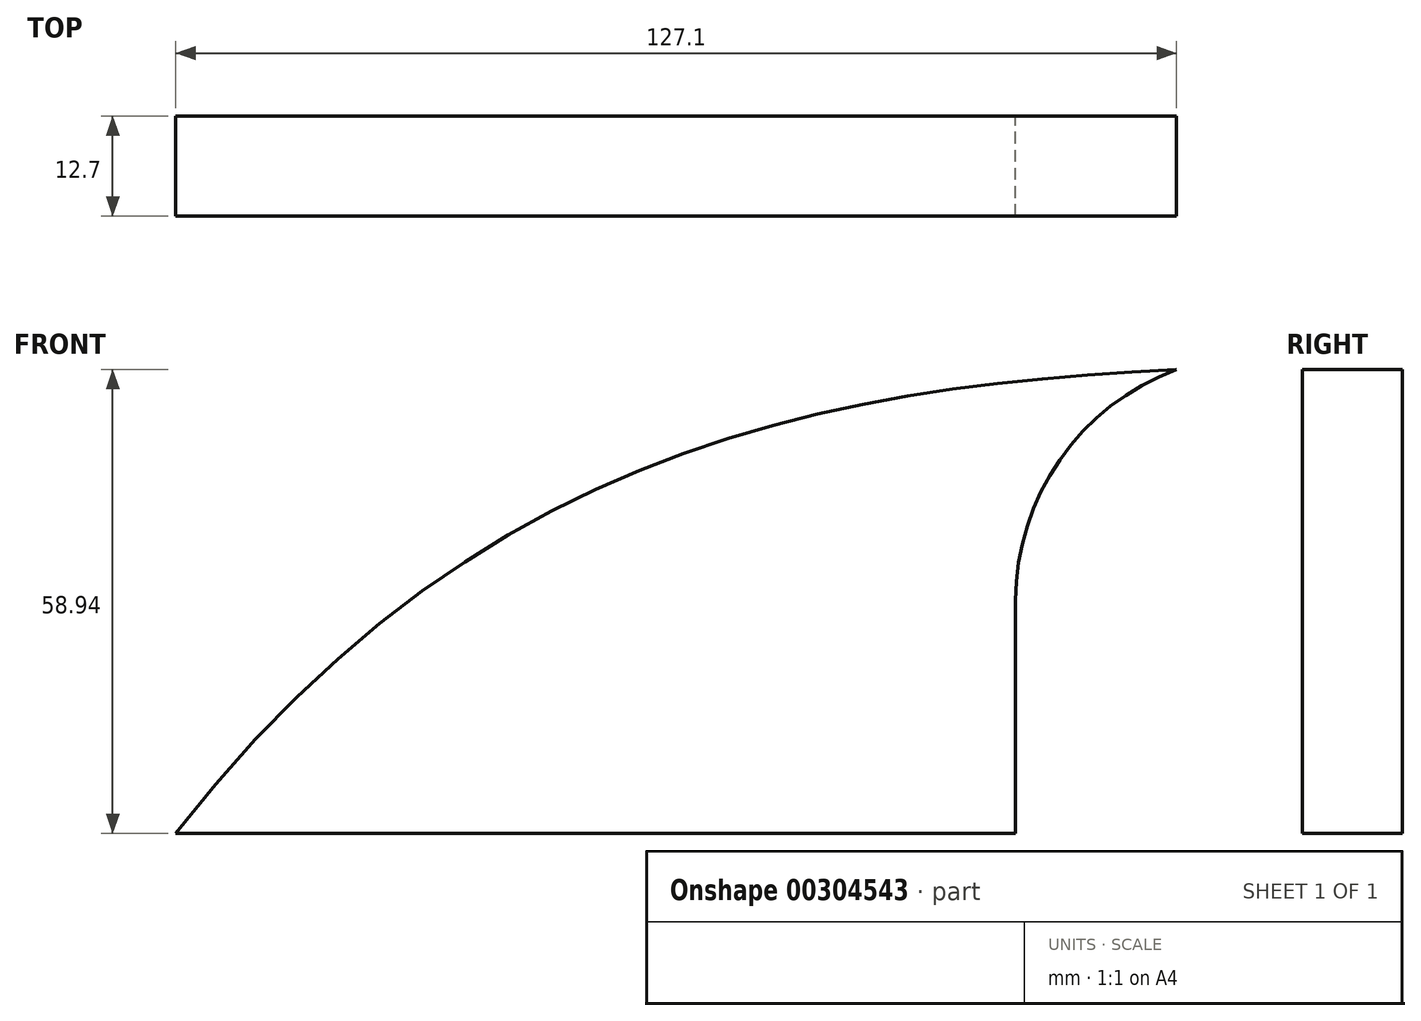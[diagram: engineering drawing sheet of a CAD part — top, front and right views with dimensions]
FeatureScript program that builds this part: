
annotation { "Feature Type Name" : "Feature", "Feature Type Description" : "" }
export const myFeature = defineFeature(function(context is Context, id is Id, definition is map)
    precondition{}
    {
        {
            var Q0;
            Q0=qCreatedBy(makeId("Front.planeOp"),FACE);
            var sketch = newSketch(context, id + "F0", { "sketchPlane" : qUnion([Q0])});
            skLineSegment(sketch, "E0.bottom", {"start": v(63.5, 25.4) * mm, "end": v(-63.5, 25.4) * mm});
            skLineSegment(sketch, "E0.top", {"start": v(63.5, -25.4) * mm, "end": v(-63.5, -25.4) * mm});
            skLineSegment(sketch, "E0.left", {"start": v(63.5, 25.4) * mm, "end": v(63.5, -25.4) * mm});
            skLineSegment(sketch, "E0.right", {"start": v(-63.5, 25.4) * mm, "end": v(-63.5, -25.4) * mm});
            skPoint(sketch, "E0.middle", {"position": v(0, 0) * mm});
            skLineSegment(sketch, "E1.bottom", {"start": v(201.55, 89.46) * mm, "end": v(131.27, 89.46) * mm});
            skLineSegment(sketch, "E1.top", {"start": v(201.55, 51.36) * mm, "end": v(131.27, 51.36) * mm});
            skLineSegment(sketch, "E1.left", {"start": v(201.55, 89.46) * mm, "end": v(201.55, 51.36) * mm});
            skLineSegment(sketch, "E1.right", {"start": v(131.27, 89.46) * mm, "end": v(131.27, 51.36) * mm});
            skPoint(sketch, "E1.middle", {"position": v(166.4, 70.4) * mm});
            skLineSegment(sketch, "E2", {"start": v(63.5, 25.4) * mm, "end": v(63.5, 54.98) * mm});
            skArc(sketch, "E3", {"start": v(63.5, 54.98) * mm, "mid": v(67.55, 63.5) * mm, "end": v(76.72, 65.76) * mm});
            skLineSegment(sketch, "E4", {"start": v(76.72, 65.76) * mm, "end": v(135.87, 65.76) * mm});
            skLineSegment(sketch, "E5.0", {"start": v(78.25, 86.08) * mm, "end": v(135.87, 86.08) * mm});
            skArc(sketch, "E5.1", {"start": v(43.18, 54.98) * mm, "mid": v(53.72, 78.42) * mm, "end": v(78.25, 86.08) * mm});
            skLineSegment(sketch, "E5.2", {"start": v(43.18, 25.4) * mm, "end": v(43.18, 54.98) * mm});
            skFitSpline(sketch, "E6", {"points": [v(-63.5, 25.4) * mm, v(131.27, 89.46) * mm], "startDerivative": vector(178.05, 230.3) * mm, "endDerivative": vector(175.75, 36.22) * mm});
            skSolve(sketch);
        }
        {
            var Q0;
            {var subQ3=sQuery(id+"F0.wireOp",EDGE,"E5.2");Q0=makeQuery(id+"F0.imprint","IMPRINT",FACE,{"disambiguationData":[TD([[makeQuery(id+"F0.imprint","IMPRINT",EDGE,{"derivedFrom":subQ3}),1.0]])]});}
            extrude(context, id + "F1", {"entities" : qUnion([Q0]), "endBound" : BoundingType.SYMMETRIC, "depth" : 12.7 * mm});
        }
    });
